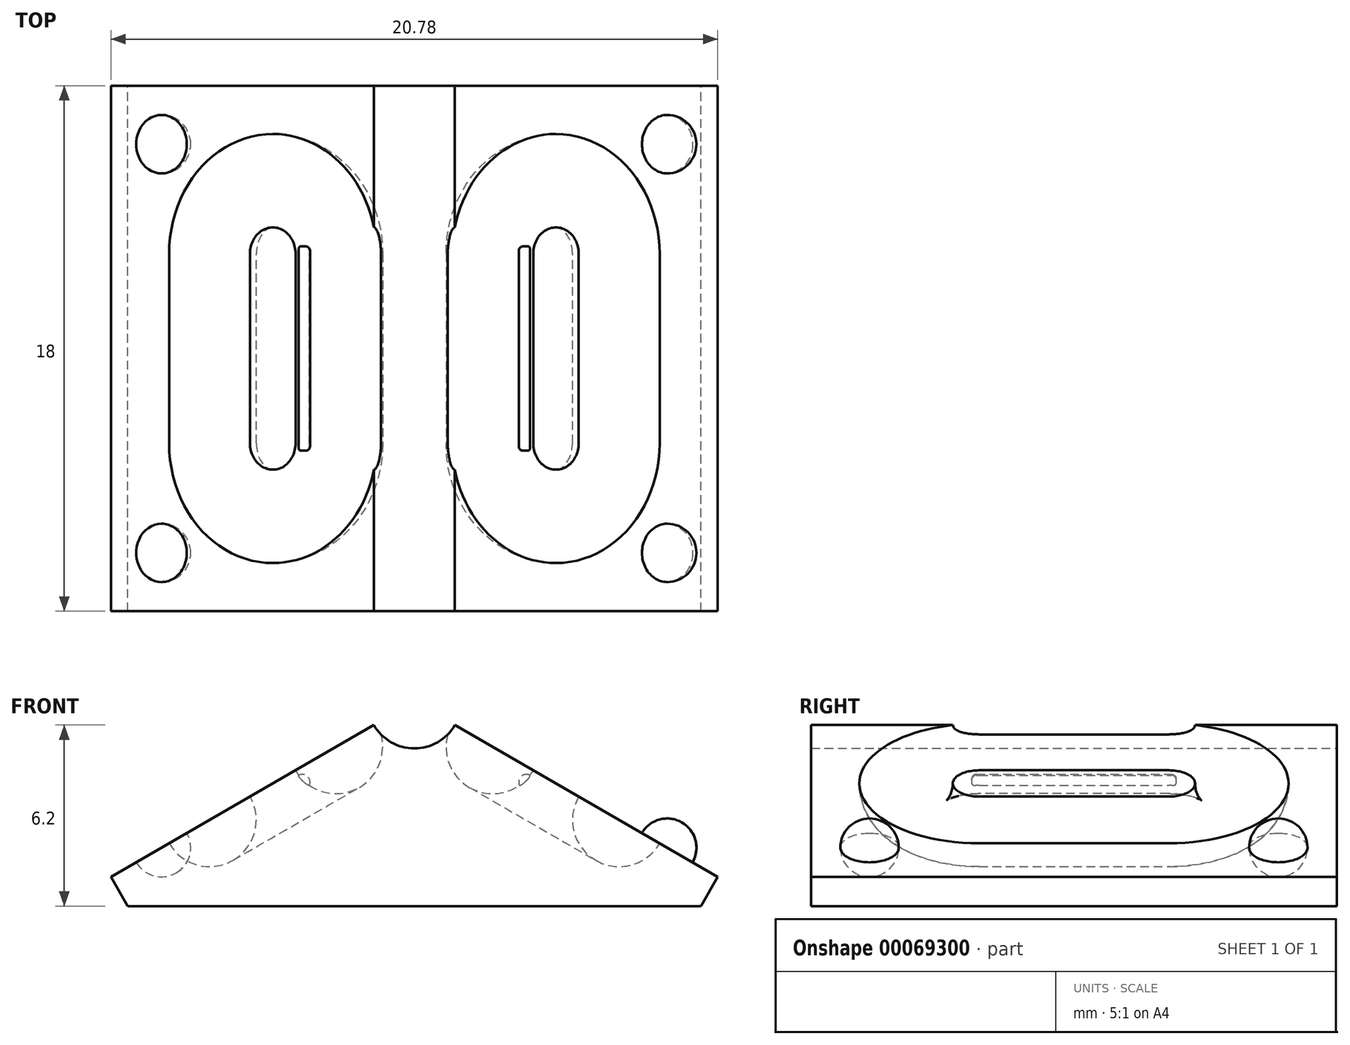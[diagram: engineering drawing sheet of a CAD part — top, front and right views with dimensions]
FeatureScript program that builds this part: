
annotation { "Feature Type Name" : "Feature", "Feature Type Description" : "" }
export const myFeature = defineFeature(function(context is Context, id is Id, definition is map)
    precondition{}
    {
        {
            var Q0;
            Q0=qCreatedBy(makeId("Front.planeOp"),FACE);
            var sketch = newSketch(context, id + "F0", { "sketchPlane" : qUnion([Q0])});
            skLineSegment(sketch, "E0", {"start": v(0, 0) * mm, "end": v(9.81, 0) * mm});
            skLineSegment(sketch, "E1", {"start": v(10.4, 1) * mm, "end": v(0, 7) * mm});
            skLineSegment(sketch, "E2", {"start": v(0, 7) * mm, "end": v(-10.4, 1) * mm});
            skLineSegment(sketch, "E3", {"start": v(-9.81, 0) * mm, "end": v(0, 0) * mm});
            skLineSegment(sketch, "E4", {"start": v(10.4, 1) * mm, "end": v(9.81, 0) * mm});
            skLineSegment(sketch, "E5.MirrorCS", {"start": v(-10.4, 1) * mm, "end": v(-9.81, 0) * mm});
            skCircle(sketch, "E6", {"center": v(0, 7) * mm, "radius": 1.6 * mm});
            skLineSegment(sketch, "E7", {"start": v(0, 7) * mm, "end": v(0, 0) * mm});
            skSolve(sketch);
        }
        {
            var Q0;
            Q0=makeQuery(id+"F0.imprint","IMPRINT",FACE,{"disambiguationData":[TD([[makeQuery(id+"F0.imprint","IMPRINT",EDGE,{"derivedFrom":sQuery(id+"F0.wireOp",EDGE,"E0")}),1.0]])]});
            extrude(context, id + "F1", {"entities" : qUnion([Q0]), "endBound" : BoundingType.SYMMETRIC, "depth" : 18 * mm});
        }
        {
            var Q0;
            Q0=makeQuery(id+"F1.opExtrude","SWEPT_FACE",FACE,{"disambiguationData":[OSD([sQuery(id+"F0.wireOp",EDGE,"E1")])]});
            var sketch = newSketch(context, id + "F2", { "sketchPlane" : qUnion([Q0])});
            skLineSegment(sketch, "E8", {"start": v(-0.4, 0) * mm, "end": v(-0.4, 3.25) * mm});
            skLineSegment(sketch, "E9", {"start": v(4.6, 3.25) * mm, "end": v(4.6, 0) * mm});
            skArc(sketch, "E10", {"start": v(4.6, 3.25) * mm, "mid": v(2.1, 5.75) * mm, "end": v(-0.4, 3.25) * mm});
            skLineSegment(sketch, "E11.MirrorCS", {"start": v(-0.4, 0) * mm, "end": v(-0.4, -3.25) * mm});
            skArc(sketch, "E12.MirrorCS", {"start": v(4.6, -3.25) * mm, "mid": v(2.1, -5.75) * mm, "end": v(-0.4, -3.25) * mm});
            skLineSegment(sketch, "E13.MirrorCS", {"start": v(4.6, -3.25) * mm, "end": v(4.6, 0) * mm});
            skSolve(sketch);
        }
        {
            var Q0;
            Q0=qCreatedBy(makeId("Front.planeOp"),FACE);
            var sketch = newSketch(context, id + "F3", { "sketchPlane" : qUnion([Q0])});
            skCircle(sketch, "E14", {"center": v(2.68, 5.45) * mm, "radius": 1.6 * mm});
            skSolve(sketch);
        }
        {
            var Q0;
            Q0=makeQuery(id+"F3.imprint","IMPRINT",FACE,{"disambiguationData":[TD([[makeQuery(id+"F3.imprint","IMPRINT",EDGE,{"derivedFrom":sQuery(id+"F3.wireOp",EDGE,"E14")}),1.0]])]});
            var Q1;
            Q1=sQuery(id+"F2.wireOp",EDGE,"E11.MirrorCS");
            var Q2;
            Q2=sQuery(id+"F2.wireOp",EDGE,"E12.MirrorCS");
            var Q3;
            Q3=sQuery(id+"F2.wireOp",EDGE,"E13.MirrorCS");
            var Q4;
            Q4=sQuery(id+"F2.wireOp",EDGE,"E9");
            var Q5;
            Q5=sQuery(id+"F2.wireOp",EDGE,"E10");
            var Q6;
            Q6=sQuery(id+"F2.wireOp",EDGE,"E8");
            sweep(context, id + "F4", {"operationType" : NewBodyOperationType.REMOVE, "profiles" : qUnion([Q0]), "path" : qUnion([Q1, Q2, Q3, Q4, Q5, Q6])});
        }
        {
            var Q0;
            Q0=qCreatedBy(makeId("Front.planeOp"),FACE);
            var sketch = newSketch(context, id + "F5", { "sketchPlane" : qUnion([Q0])});
            skLineSegment(sketch, "E15.0", {"start": v(1.39, 6.2) * mm, "end": v(1.39, 6.2) * mm});
            skLineSegment(sketch, "E16.0", {"start": v(10.4, 1) * mm, "end": v(1.39, 6.2) * mm, "construction": true});
            skLineSegment(sketch, "E17", {"start": v(4.07, 4.65) * mm, "end": v(3.32, 3.34) * mm, "construction": true});
            skCircle(sketch, "E18", {"center": v(3.84, 4.24) * mm, "radius": 0.27 * mm});
            skLineSegment(sketch, "E19", {"start": v(0.2, 7.36) * mm, "end": v(0, 7) * mm, "construction": true});
            skCircle(sketch, "E20", {"center": v(2.6, 5.5) * mm, "radius": 1.5 * mm, "construction": true});
            skSolve(sketch);
        }
        {
            var Q0;
            Q0=makeQuery(id+"F5.imprint","IMPRINT",FACE,{"disambiguationData":[TD([[makeQuery(id+"F5.imprint","IMPRINT",EDGE,{"derivedFrom":sQuery(id+"F5.wireOp",EDGE,"E18")}),1.0]])]});
            extrude(context, id + "F6", {"entities" : qUnion([Q0]), "operationType" : NewBodyOperationType.ADD, "endBound" : BoundingType.SYMMETRIC, "depth" : 7 * mm});
        }
        {
            var Q0;
            Q0=makeQuery(id+"F6.opExtrude","CAP_EDGE",EDGE,{"disambiguationData":[OSD([sQuery(id+"F5.wireOp",EDGE,"E18")])],"isStart":false});
            var Q1;
            Q1=makeQuery(id+"F6.opExtrude","CAP_EDGE",EDGE,{"disambiguationData":[OSD([sQuery(id+"F5.wireOp",EDGE,"E18")])],"isStart":true});
            fillet(context, id + "F7", {"entities" : qUnion([Q0, Q1]), "radius" : 0.15 * mm, "allowEdgeOverflow" : false});
        }
        {
            var Q0;
            Q0=makeQuery(id+"F1.opExtrude","SWEPT_BODY",BODY,{"disambiguationData":[OSD([sQuery(id+"F0.wireOp",EDGE,"E0"),sQuery(id+"F0.wireOp",EDGE,"E1"),sQuery(id+"F0.wireOp",EDGE,"E4"),sQuery(id+"F0.wireOp",EDGE,"E6"),sQuery(id+"F0.wireOp",EDGE,"E7")])]});
            var Q1;
            Q1=qCreatedBy(makeId("Right.planeOp"),FACE);
            mirror(context, id + "F8", {"operationType" : NewBodyOperationType.ADD, "entities" : qUnion([Q0]), "mirrorPlane" : qUnion([Q1])});
        }
        {
            var Q0;
            {var subQ1=sQuery(id+"F0.wireOp",EDGE,"E4");var subQ3=sQuery(id+"F0.wireOp",EDGE,"E1");Q0=makeQuery(id+"F4.boolean.opBoolean","SPLIT",FACE,{"disambiguationData":[TD([makeQuery(id+"F1.opExtrude","SWEPT_FACE",FACE,{"disambiguationData":[OSD([subQ1])]})])],"derivedFrom":makeQuery(id+"F1.opExtrude","SWEPT_FACE",FACE,{"disambiguationData":[OSD([subQ3])]})});}
            var sketch = newSketch(context, id + "F9", { "sketchPlane" : qUnion([Q0])});
            skCircle(sketch, "E21", {"center": v(6.5, 7) * mm, "radius": 1 * mm});
            skCircle(sketch, "E22.MirrorC", {"center": v(6.5, -7) * mm, "radius": 1 * mm});
            skSolve(sketch);
        }
        {
            var Q0;
            Q0 = qSketchRegion(id + "F9", true);
            extrude(context, id + "F10", {"entities" : qUnion([Q0]), "operationType" : NewBodyOperationType.ADD, "depth" : 1 * mm});
        }
        {
            var Q0;
            Q0=makeQuery(id+"F10.opExtrude","CAP_EDGE",EDGE,{"disambiguationData":[OSD([sQuery(id+"F9.wireOp",EDGE,"E21")])],"isStart":false});
            var Q1;
            Q1=makeQuery(id+"F10.opExtrude","CAP_EDGE",EDGE,{"disambiguationData":[OSD([sQuery(id+"F9.wireOp",EDGE,"E22.MirrorC")])],"isStart":false});
            fillet(context, id + "F11", {"entities" : qUnion([Q0, Q1]), "radius" : 1 * mm, "tangentPropagation" : true, "allowEdgeOverflow" : false});
        }
        {
            var Q0;
            {var subQ1=sQuery(id+"F0.wireOp",EDGE,"E4");var subQ3=sQuery(id+"F0.wireOp",EDGE,"E1");Q0=makeQuery(id+"F8.opPattern","COPY",FACE,{"derivedFrom":makeQuery(id+"F4.boolean.opBoolean","SPLIT",FACE,{"disambiguationData":[TD([makeQuery(id+"F1.opExtrude","SWEPT_FACE",FACE,{"disambiguationData":[OSD([subQ1])]})])],"derivedFrom":makeQuery(id+"F1.opExtrude","SWEPT_FACE",FACE,{"disambiguationData":[OSD([subQ3])]})}),"instanceName":"1"});}
            var sketch = newSketch(context, id + "F12", { "sketchPlane" : qUnion([Q0])});
            skCircle(sketch, "E23", {"center": v(-6.5, 7) * mm, "radius": 1 * mm});
            skCircle(sketch, "E24.MirrorC", {"center": v(-6.5, -7) * mm, "radius": 1 * mm});
            skSolve(sketch);
        }
        {
            var Q0;
            Q0 = qSketchRegion(id + "F12", true);
            extrude(context, id + "F13", {"entities" : qUnion([Q0]), "operationType" : NewBodyOperationType.REMOVE, "oppositeDirection" : true, "depth" : 1 * mm});
        }
        {
            var Q0;
            Q0=makeQuery(id+"F13.boolean.opBoolean","COPY",EDGE,{"derivedFrom":makeQuery(id+"F13.opExtrude","CAP_EDGE",EDGE,{"disambiguationData":[OSD([sQuery(id+"F12.wireOp",EDGE,"E23")])],"isStart":false})});
            var Q1;
            Q1=makeQuery(id+"F13.boolean.opBoolean","COPY",EDGE,{"derivedFrom":makeQuery(id+"F13.opExtrude","CAP_EDGE",EDGE,{"disambiguationData":[OSD([sQuery(id+"F12.wireOp",EDGE,"E24.MirrorC")])],"isStart":false})});
            fillet(context, id + "F14", {"entities" : qUnion([Q0, Q1]), "radius" : 1 * mm, "tangentPropagation" : true, "allowEdgeOverflow" : false});
        }
    });
